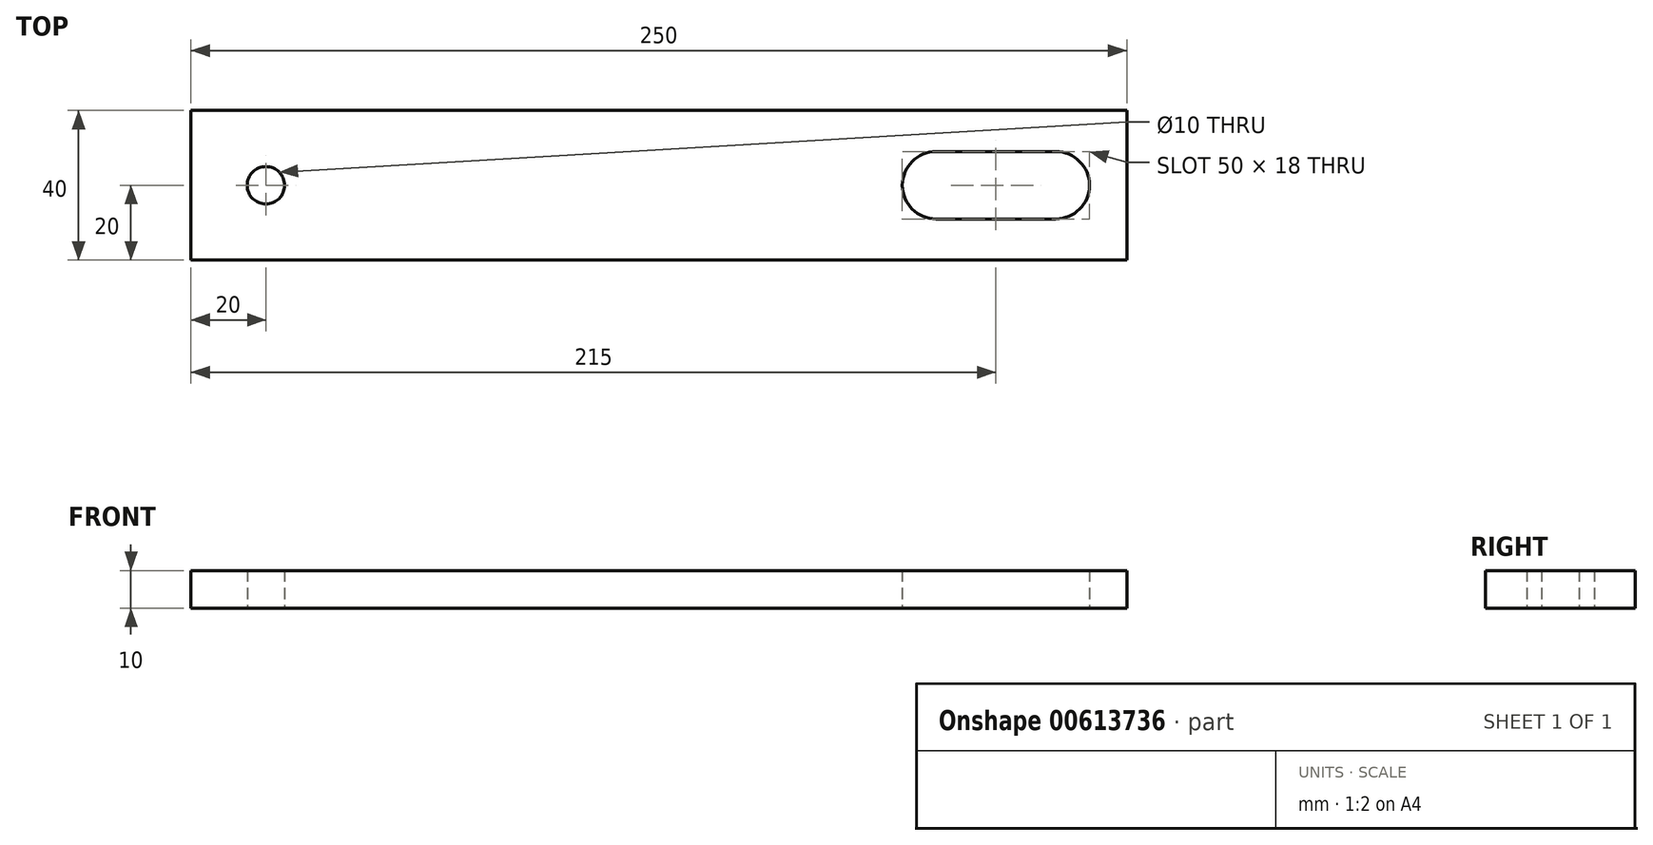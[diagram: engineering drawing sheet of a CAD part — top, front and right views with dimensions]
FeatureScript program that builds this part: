
annotation { "Feature Type Name" : "Feature", "Feature Type Description" : "" }
export const myFeature = defineFeature(function(context is Context, id is Id, definition is map)
    precondition{}
    {
        {
            var Q0;
            Q0=qCreatedBy(makeId("Top.planeOp"),FACE);
            var sketch = newSketch(context, id + "F0", { "sketchPlane" : qUnion([Q0])});
            skLineSegment(sketch, "E0.bottom", {"start": v(125, 20) * mm, "end": v(-125, 20) * mm});
            skLineSegment(sketch, "E0.top", {"start": v(125, -20) * mm, "end": v(-125, -20) * mm});
            skLineSegment(sketch, "E0.left", {"start": v(125, 20) * mm, "end": v(125, -20) * mm});
            skLineSegment(sketch, "E0.right", {"start": v(-125, 20) * mm, "end": v(-125, -20) * mm});
            skPoint(sketch, "E0.middle", {"position": v(0, 0) * mm});
            skCircle(sketch, "E1", {"center": v(-105, 0) * mm, "radius": 5 * mm});
            skSolve(sketch);
        }
        {
            var Q0;
            Q0=makeQuery(id+"F0.imprint","IMPRINT",FACE,{"disambiguationData":[TD([[makeQuery(id+"F0.imprint","IMPRINT",EDGE,{"derivedFrom":sQuery(id+"F0.wireOp",EDGE,"E0.bottom")}),1.0]])]});
            extrude(context, id + "F1", {"entities" : qUnion([Q0]), "depth" : 10 * mm, "offsetDistance" : 25 * mm});
        }
        {
            var Q0;
            Q0=makeQuery(id+"F1.opExtrude","CAP_FACE",FACE,{"disambiguationData":[OSD([sQuery(id+"F0.wireOp",EDGE,"E0.bottom"),sQuery(id+"F0.wireOp",EDGE,"E0.top"),sQuery(id+"F0.wireOp",EDGE,"E0.left"),sQuery(id+"F0.wireOp",EDGE,"E0.right"),sQuery(id+"F0.wireOp",EDGE,"E1")])],"isStart":true});
            var sketch = newSketch(context, id + "F2", { "sketchPlane" : qUnion([Q0])});
            skArc(sketch, "E2", {"start": v(106, -9) * mm, "mid": v(115, 0) * mm, "end": v(106, 9) * mm});
            skArc(sketch, "E3", {"start": v(74, 9) * mm, "mid": v(65, 0) * mm, "end": v(74, -9) * mm});
            skLineSegment(sketch, "E4", {"start": v(74, -9) * mm, "end": v(106, -9) * mm});
            skLineSegment(sketch, "E5", {"start": v(106, 9) * mm, "end": v(74, 9) * mm});
            skSolve(sketch);
        }
        {
            var Q0;
            Q0=qSketchRegion(id+"F2",true);
            extrude(context, id + "F3", {"entities" : qUnion([Q0]), "operationType" : NewBodyOperationType.REMOVE, "oppositeDirection" : true, "depth" : 25 * mm, "offsetDistance" : 25 * mm});
        }
    });
